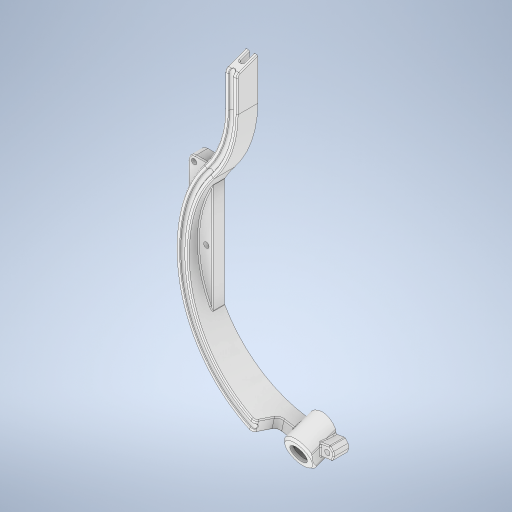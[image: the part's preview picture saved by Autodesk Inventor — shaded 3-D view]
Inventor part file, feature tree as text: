
AUTODESK INVENTOR PART (.ipt)
format: ipt  version: 2024 (Build 280153000, 153)  size: 1,185,280 bytes
history: native  units: mm
features: fillet x14, sketch x13, extrude x7, projected_geometry x6, plane x5, hole x3, other x3, thicken_offset x2, chamfer x2, sweep x1, helix x1, revolve x1
ambient origin geometry x8: Origin, YZ Plane, XZ Plane, XY Plane, X Axis, Y Axis, Z Axis, Center Point
bodies: Solid1 (feature_tree)
feature tree (58):
  thicken_offset  "Thicken1"
  sketch  "Sketch2"  dims[d5=12.0mm]
  plane  "Work Plane1"
  sweep  "Sweep1"
  helix  "Coil1"  [1 undecoded]
  chamfer  "Chamfer1"  Distance=100.0mm
  chamfer  "Chamfer2"  [1 undecoded]
  fillet  "Fillet4"  Radius=2.094395mm
  sketch  "Sketch5"  dims[d8=1.25mm d9=0.0mm d10=0.0mm]
  extrude  "Extrusion1"  Depth=4.0mm
  fillet  "Fillet5"  Radius=12.0mm
  hole  "Hole1"  [1 undecoded]
  fillet  "Fillet6"  Radius=108.0mm
  fillet  "Fillet7"  Radius=12.0mm
  sketch  "Sketch6"  dims[d11=60.0mm d12=400.0mm d13=5.0mm d14=0.0mm d15=45.0deg d16=1.745329mm d17=0.0mm d18=0.0mm d22=175.0mm d23=2.094395mm]
  extrude  "Extrusion2"  Depth=1.0mm
  fillet  "Fillet8"  Radius=1.0mm
  plane  "Work Plane7"
  extrude  "Extrusion11"  Depth=15.0mm TaperAngle=0.0deg
  fillet  "Fillet24"  Radius=6.0mm
  plane  "Work Plane8"
  other  "Work Axis1"
  revolve  "Revolution1"  [1 undecoded]
  sketch  "Sketch19"  dims[d35=7.5mm]
  hole  "Hole2"  [1 undecoded]
  extrude  "Extrusion12"  Depth=1.0mm TaperAngle=0.0deg
  fillet  "Fillet25"  Radius=3.0mm
  fillet  "Fillet26"  Radius=2.0mm
  fillet  "Fillet27"  Radius=2.0mm
  fillet  "Fillet28"  [1 undecoded]
  fillet  "Fillet29"  Radius=40.0mm
  plane  "Work Plane9"
  extrude  "Extrusion13"  TaperAngle=0.0deg  [1 undecoded]
  fillet  "Fillet30"  Radius=4.0mm
  hole  "Hole3"  [1 undecoded]
  thicken_offset  "Thicken2"
  fillet  "Fillet31"  Radius=1.0mm
  fillet  "Fillet32"  Radius=1.0mm
  sketch  "Sketch23"  dims[d113=30.0mm d114=2.0mm d115=15.0mm d116=0.0mm d117=3.0mm d122=2.0mm d123=2.0mm d124=90.0deg d125=40.0mm d126=5.3mm d127=6.0mm d128=4.0mm d129=2.0mm d130=90.0deg d131=8.0mm d132=20.594885mm d133=0.0mm d134=0.0mm d135=4.0mm d136=1.0mm d137=1.0mm d138=1.0mm d139=0.5mm d140=-3.0mm d142=0.0mm d143=0.0mm d144=0.5mm d145=16.4mm d146=6.0mm d147=4.0mm d148=2.0mm d149=90.0deg d150=8.0mm d151=20.594885mm d152=2.0mm d153=10.0mm d154=0.0mm d155=4.0mm d156=1.0mm d157=1.0mm d158=102.0mm d159=65.0mm d160=65.0mm d161=12.0mm d162=116.0mm d163=20.0mm]
  sketch  "Sketch1"  dims[d0=116.0mm d1=69.5mm d2=100.0mm d3=100.0mm d4=0.0mm]
  other  "Srf1"
  projected_geometry  "Projected Loop1"
  sketch  "Sketch3"  dims[d6=4.4mm]
  sketch  "Sketch4"  dims[d7=19.0mm]
  projected_geometry  "Projected Loop2"
  projected_geometry  "Projected Loop3"
  projected_geometry  "Projected Loop4"
  plane  "Work Plane6"
  sketch  "Sketch16"  dims[d24=20.25mm d25=2.0mm d26=3.490659mm d27=4.0mm d28=12.0mm]
  sketch  "Sketch17"  dims[d30=130.0mm d31=12.0mm d32=108.0mm d33=12.0mm d34=0.0mm]
  sketch  "Sketch20"  dims[d36=5.3mm d37=6.0mm d38=4.0mm d39=2.0mm d40=90.0deg d41=8.0mm d42=20.594885mm d43=1.0mm d44=1.0mm]
  sketch  "Sketch21"  dims[d45=30.0mm d46=2.0mm d47=3.490659mm d50=15.0mm d51=0.0mm d52=6.0mm]
  sketch  "Sketch22"  dims[d110=13.5mm d111=3.490659mm d112=-24.0mm]
  other  "Srf2"
  extrude  "ExtrusionSrf1"  Depth=1.0mm
  extrude  "ExtrusionSrf2"  [1 undecoded]
  projected_geometry  "Project Cut Edges3"
  projected_geometry  "Project Cut Edges4"
note: 9 required parameter values undecoded (feature->parameter linkage not recoverable at this tier; creation-order binding heuristic only, values carry confidence <= 0.55)